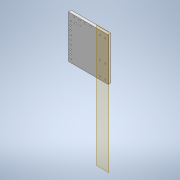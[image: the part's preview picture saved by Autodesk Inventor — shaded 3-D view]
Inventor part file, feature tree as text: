
AUTODESK INVENTOR PART (.ipt)
format: ipt  version: 2022 (Build 260153000, 153)  size: 166,400 bytes
history: native  units: in
note: dims shown in document units (in); Inventor stores cm internally (conversion verified against a paired STEP export)
features: other x6, sketch x3, extrude x2, reference x2, plane x1
ambient origin geometry x8: Origin, YZ Plane, XZ Plane, XY Plane, X Axis, Y Axis, Z Axis, Center Point
bodies: Solid1 (feature_tree)
feature tree (14):
  other  "backboard.ipt"
  extrude  "Extrusion1"  Depth=0.3937in TaperAngle=0.0deg
  extrude  "Extrusion2"  Depth=0.1693in
  other  "Solid1::backboard.ipt"
  other  "TaggingFeature1"
  sketch  "Sketch1"  dims[d0=0.3937in d1=2.1614in d2=0.0in]
  plane  "Work Plane1"
  sketch  "Sketch2"  dims[d3=0.1693in d4=0.1693in]
  reference  "Reference1"
  sketch  "Sketch3"  dims[d5=0.3937in d6=0.0in d7=0.0in d8=1.9685in d10=0.5906in d11=0.3937in d13=0.3937in]
  reference  "Reference2"
  other  "Linear Rail Assembly.iam"
  other  "backboard:1"
  other  "Lower Support_MIR:1"
